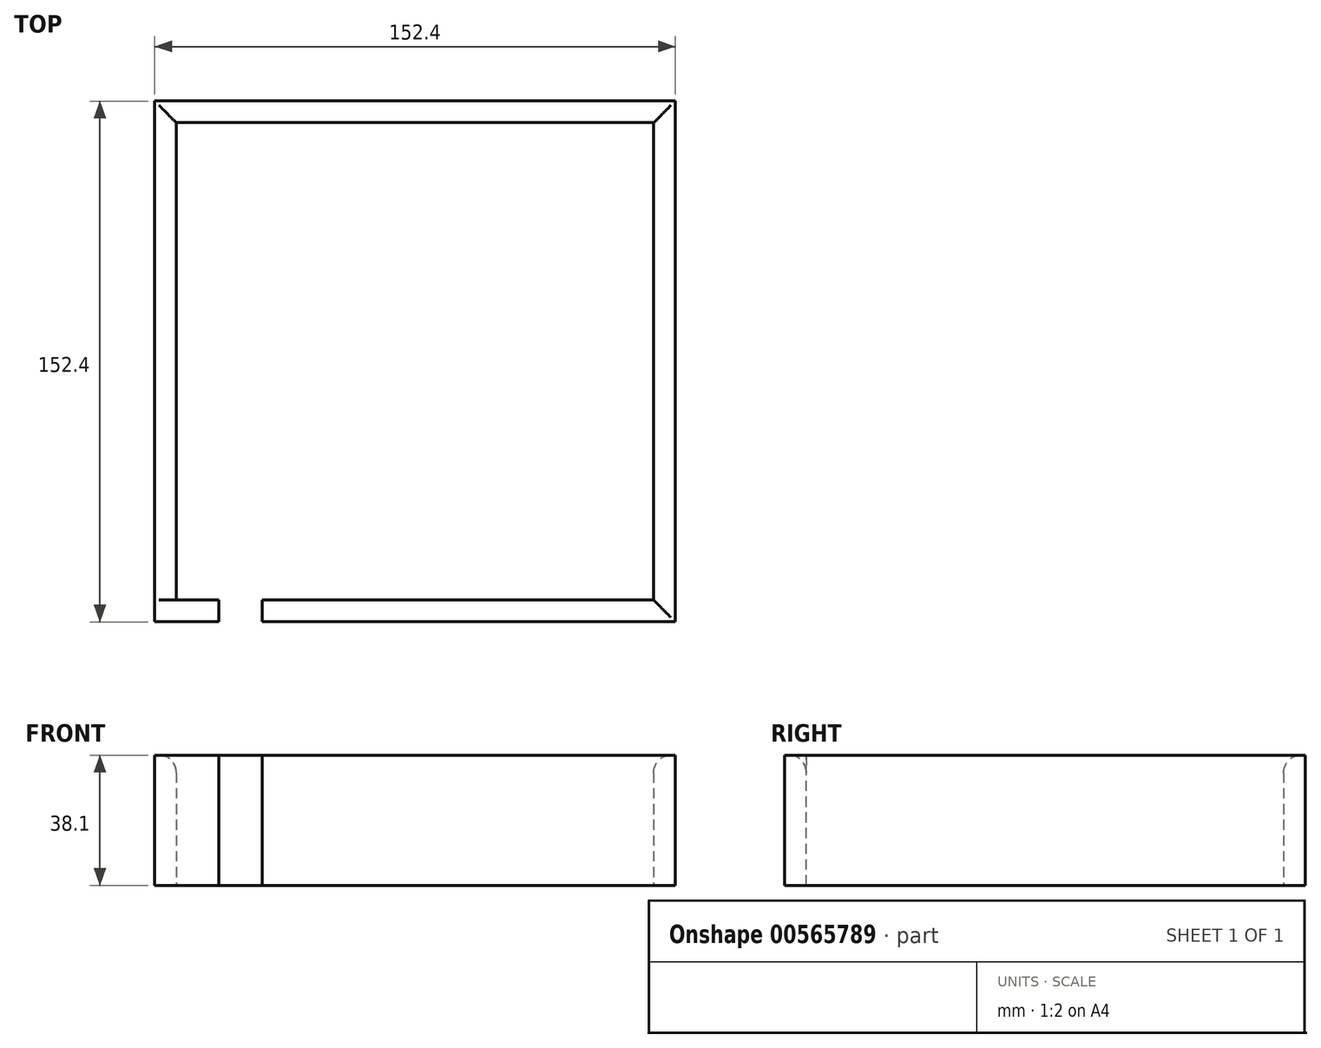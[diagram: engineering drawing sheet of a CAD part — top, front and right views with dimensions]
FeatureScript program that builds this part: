
annotation { "Feature Type Name" : "Feature", "Feature Type Description" : "" }
export const myFeature = defineFeature(function(context is Context, id is Id, definition is map)
    precondition{}
    {
        {
            var Q0;
            Q0=qCreatedBy(makeId("Top.planeOp"),FACE);
            var sketch = newSketch(context, id + "F0", { "sketchPlane" : qUnion([Q0])});
            skLineSegment(sketch, "E0.bottom", {"start": v(-76.2, 68.72) * mm, "end": v(76.2, 68.72) * mm});
            skLineSegment(sketch, "E0.top", {"start": v(-76.2, -83.68) * mm, "end": v(76.2, -83.68) * mm});
            skLineSegment(sketch, "E0.left", {"start": v(-76.2, 68.72) * mm, "end": v(-76.2, -83.68) * mm});
            skLineSegment(sketch, "E0.right", {"start": v(76.2, 68.72) * mm, "end": v(76.2, -83.68) * mm});
            skLineSegment(sketch, "E1.0", {"start": v(-69.85, 62.37) * mm, "end": v(-69.85, -77.33) * mm});
            skLineSegment(sketch, "E1.1", {"start": v(-69.85, 62.37) * mm, "end": v(69.85, 62.37) * mm});
            skLineSegment(sketch, "E1.2", {"start": v(69.85, 62.37) * mm, "end": v(69.85, -77.33) * mm});
            skLineSegment(sketch, "E1.3", {"start": v(-69.85, -77.33) * mm, "end": v(69.85, -77.33) * mm});
            skSolve(sketch);
        }
        {
            var Q0;
            Q0=makeQuery(id+"F0.imprint","IMPRINT",FACE,{"disambiguationData":[TD([[makeQuery(id+"F0.imprint","IMPRINT",EDGE,{"derivedFrom":sQuery(id+"F0.wireOp",EDGE,"E0.bottom")}),-1.0]])]});
            extrude(context, id + "F1", {"entities" : qUnion([Q0]), "depth" : 38.1 * mm});
        }
        {
            var Q0;
            Q0=makeQuery(id+"F1.opExtrude","SWEPT_FACE",FACE,{"disambiguationData":[OSD([sQuery(id+"F0.wireOp",EDGE,"E0.top")])]});
            var sketch = newSketch(context, id + "F2", { "sketchPlane" : qUnion([Q0])});
            skLineSegment(sketch, "E2.bottom", {"start": v(-57.4, 38.1) * mm, "end": v(-44.7, 38.1) * mm});
            skLineSegment(sketch, "E2.top", {"start": v(-57.4, 0) * mm, "end": v(-44.7, 0) * mm});
            skLineSegment(sketch, "E2.left", {"start": v(-57.4, 38.1) * mm, "end": v(-57.4, 0) * mm});
            skLineSegment(sketch, "E2.right", {"start": v(-44.7, 38.1) * mm, "end": v(-44.7, 0) * mm});
            skSolve(sketch);
        }
        {
            var Q0;
            Q0=makeQuery(id+"F2.imprint","IMPRINT",FACE,{"disambiguationData":[TD([[makeQuery(id+"F2.imprint","IMPRINT",EDGE,{"derivedFrom":sQuery(id+"F2.wireOp",EDGE,"E2.bottom")}),-1.0]])]});
            extrude(context, id + "F3", {"entities" : qUnion([Q0]), "operationType" : NewBodyOperationType.REMOVE, "oppositeDirection" : true, "depth" : 37.08 * mm});
        }
        {
            var Q0;
            Q0=makeQuery(id+"F1.opExtrude","CAP_EDGE",EDGE,{"disambiguationData":[OSD([sQuery(id+"F0.wireOp",EDGE,"E1.2")])],"isStart":false});
            var Q1;
            Q1=makeQuery(id+"F1.opExtrude","CAP_EDGE",EDGE,{"disambiguationData":[OSD([sQuery(id+"F0.wireOp",EDGE,"E1.1")])],"isStart":false});
            var Q2;
            {var subQ0=sQuery(id+"F0.wireOp",EDGE,"E1.3");var subQ1=sQuery(id+"F0.wireOp",EDGE,"E1.2");Q2=makeQuery(id+"F3.boolean.opBoolean","SPLIT",EDGE,{"disambiguationData":[TD([makeQuery(id+"F1.opExtrude","SWEPT_FACE",FACE,{"disambiguationData":[OSD([subQ1])]})])],"derivedFrom":makeQuery(id+"F1.opExtrude","CAP_EDGE",EDGE,{"disambiguationData":[OSD([subQ0])],"isStart":false})});}
            var Q3;
            Q3=makeQuery(id+"F1.opExtrude","CAP_EDGE",EDGE,{"disambiguationData":[OSD([sQuery(id+"F0.wireOp",EDGE,"E1.0")])],"isStart":false});
            fillet(context, id + "F4", {"entities" : qUnion([Q0, Q1, Q2, Q3]), "radius" : 5.08 * mm, "tangentPropagation" : true, "allowEdgeOverflow" : false});
        }
    });
